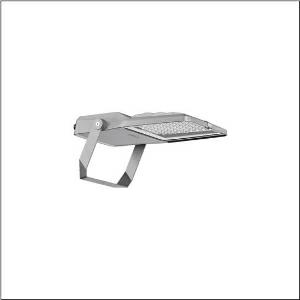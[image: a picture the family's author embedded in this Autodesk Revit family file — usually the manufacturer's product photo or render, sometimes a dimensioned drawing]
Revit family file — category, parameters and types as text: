
# Revit family: floodlight_fl_21_mini___pl61_5xa7776d4c1a_545e
name_source: partatom
category: Lighting Fixtures
units: mm (PartAtom-declared; Revit-internal decimal feet)

## family parameters
Cut with Voids When Loaded = No
Host = Face
Light Source = No
Part Type = Normal
Room Calculation Point = No
Round Connector Dimension = Use Diameter
Shared = No

## types (1)
- --- (1 x LED, 18260 lm, 142.9 W, 4000K)
    Apparent Load = 143 VA
    CIE Flux Codes = 33 65 98 100 100
    Color Rendering = 70
    Color Temperature = 4000K
    Default Elevation = 1800 mm
    Description = Floodlight FL 21 mini, floodlight, primary light control with lens, of PMMA, primary optical cover: protective disc, of toughened safety glass, transparent, light distribution: PL61, light emission: direct distribution, installation type: surface-mounted, LED, High Power LED, rated luminous flux: 18.260lm, luminous efficacy: 128lm/W, light colour: 740, colour temperature: 4000K, control gear: D4iSmart Interface (Zhaga), control: overheat protection, constant luminous flux control, time-dependent luminous flux control, flexible luminous flux parameterisation, pre-setting: logarithmic dimming characteristic, with terminal, 6-pole, mains connection: 220..240V, AC, 50/60Hz, start of lifetime: 143W, end of service life: 151W, reduction: 63W, mounting bracket, of diecast aluminium, powder-coated, Siteco® metallic grey (DB 702S), corrosivity category C5 mid according to DIN EN ISO 12944, suitable for swimming pools, chlorine-resistant, sealing non-destructively replaceable, mounting bracket, of steel, galvanised, powder-coated, Siteco® metallic grey (DB 702S), Smart Interface below and above, protection rating (complete): IP66, insulation class (complete): insulation class II (safety insulation), certification: CE, ENEC, VDE, protection symbol: D, impact resistance: IK08, permissible operating ambient temperature: -40..+40°C, permissible operating ambient temperature for outdoor applications: -40..+50°C, standard: DIN EN 12944, LABS conformity tested according to VDMA 24364:2018-05, packaging unit: 1 piece

Light Distribution: PL61
    Height = 70 mm
    Lamp = 1 x LED
    Lamp Light Flux = 18260 lm
    Lamp Power = 142.9 W
    Lamp count = 1
    Length = 485 mm
    Luminous efficacy = 128 lm/W
    Manufacturer = Siteco
    ModVariant = No
    Model = 5XA7776D4C1A
    Number of Poles = 1
    OnlyDefault = Yes
    Power Factor = 1
    Product Name = Floodlight FL 21 mini | PL61
    Product group = floodlight | pylon annexe
    ProductGroupID = 6200
    Protection Class = Protection class II
    Protection Degree = IP 66
    RLX_Detail_Level = 1
    RLX_Emergency_Light_Flux = 0 lm
    RLX_Emergency_Type = 0
    RLX_Emergency_Type_DB = No
    RlxData = <blob elided: 96381 chars, md5=ac340c24>
    Socket = socket
    Standby Power = 0 W
    System Light Flux = 18260 lm
    System Power = 143 W
    Type Comments = factory setting: luminous flux: 100 % | dim-lin: 254 | 730 mA
    Type Image = l_1006845.jpg
    URL = http://relux.com
    VarID = @adj_100512
    Voltage = 0 V
    Weight = 0.00 kg
    Width = 337 mm

## geometry (parser evidence)
native form markers: Blend x4, Sweep x10
no freeform markers — native parametric forms only
